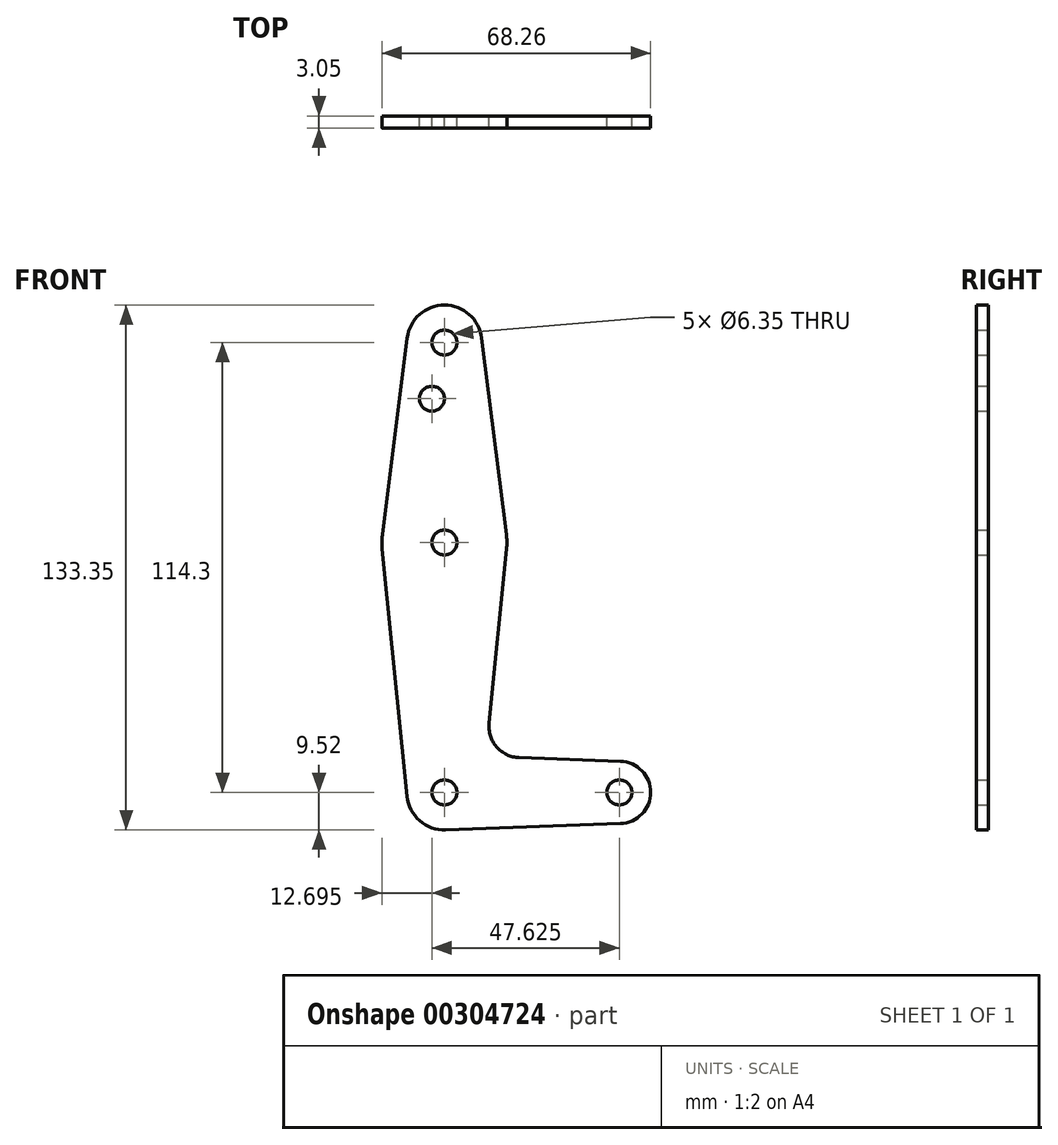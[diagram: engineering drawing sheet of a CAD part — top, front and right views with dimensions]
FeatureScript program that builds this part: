
annotation { "Feature Type Name" : "Feature", "Feature Type Description" : "" }
export const myFeature = defineFeature(function(context is Context, id is Id, definition is map)
    precondition{}
    {
        {
            var Q0;
            Q0=qCreatedBy(makeId("Front.planeOp"),FACE);
            var sketch = newSketch(context, id + "F0", { "sketchPlane" : qUnion([Q0])});
            skLineSegment(sketch, "E0", {"start": v(0, 0) * mm, "end": v(0, 114.3) * mm, "construction": true});
            skLineSegment(sketch, "E1", {"start": v(0, 0) * mm, "end": v(44.45, 0) * mm, "construction": true});
            skCircle(sketch, "E2", {"center": v(0, 0) * mm, "radius": 9.53 * mm});
            skCircle(sketch, "E3", {"center": v(0, 63.5) * mm, "radius": 15.88 * mm});
            skCircle(sketch, "E4", {"center": v(0, 114.3) * mm, "radius": 9.53 * mm});
            skCircle(sketch, "E5", {"center": v(44.45, 0) * mm, "radius": 7.94 * mm});
            skLineSegment(sketch, "E6", {"start": v(9.45, 115.5) * mm, "end": v(15.75, 65.48) * mm});
            skLineSegment(sketch, "E7", {"start": v(-9.45, 115.5) * mm, "end": v(-15.75, 65.48) * mm});
            skLineSegment(sketch, "E8", {"start": v(-15.8, 61.91) * mm, "end": v(-9.48, -0.95) * mm});
            skLineSegment(sketch, "E9", {"start": v(18.97, 8.85) * mm, "end": v(44.73, 7.93) * mm});
            skLineSegment(sketch, "E10", {"start": v(0.34, -9.52) * mm, "end": v(44.73, -7.93) * mm});
            skLineSegment(sketch, "E11", {"start": v(15.8, 61.91) * mm, "end": v(11.34, 17.6) * mm});
            skCircle(sketch, "E12", {"center": v(0, 114.3) * mm, "radius": 3.18 * mm});
            skCircle(sketch, "E13", {"center": v(0, 63.5) * mm, "radius": 3.18 * mm});
            skCircle(sketch, "E14", {"center": v(0, 0) * mm, "radius": 3.18 * mm});
            skCircle(sketch, "E15", {"center": v(44.45, 0) * mm, "radius": 3.18 * mm});
            skCircle(sketch, "E16", {"center": v(-3.18, 100.03) * mm, "radius": 3.18 * mm});
            skArc(sketch, "E17.filletArc", {"start": v(11.34, 17.6) * mm, "mid": v(13.26, 11.57) * mm, "end": v(18.97, 8.85) * mm});
            skSolve(sketch);
        }
        {
            var Q0;
            Q0 = qSketchRegion(id + "F0", true);
            extrude(context, id + "F1", {"entities" : qUnion([Q0]), "depth" : 3.05 * mm});
        }
    });
